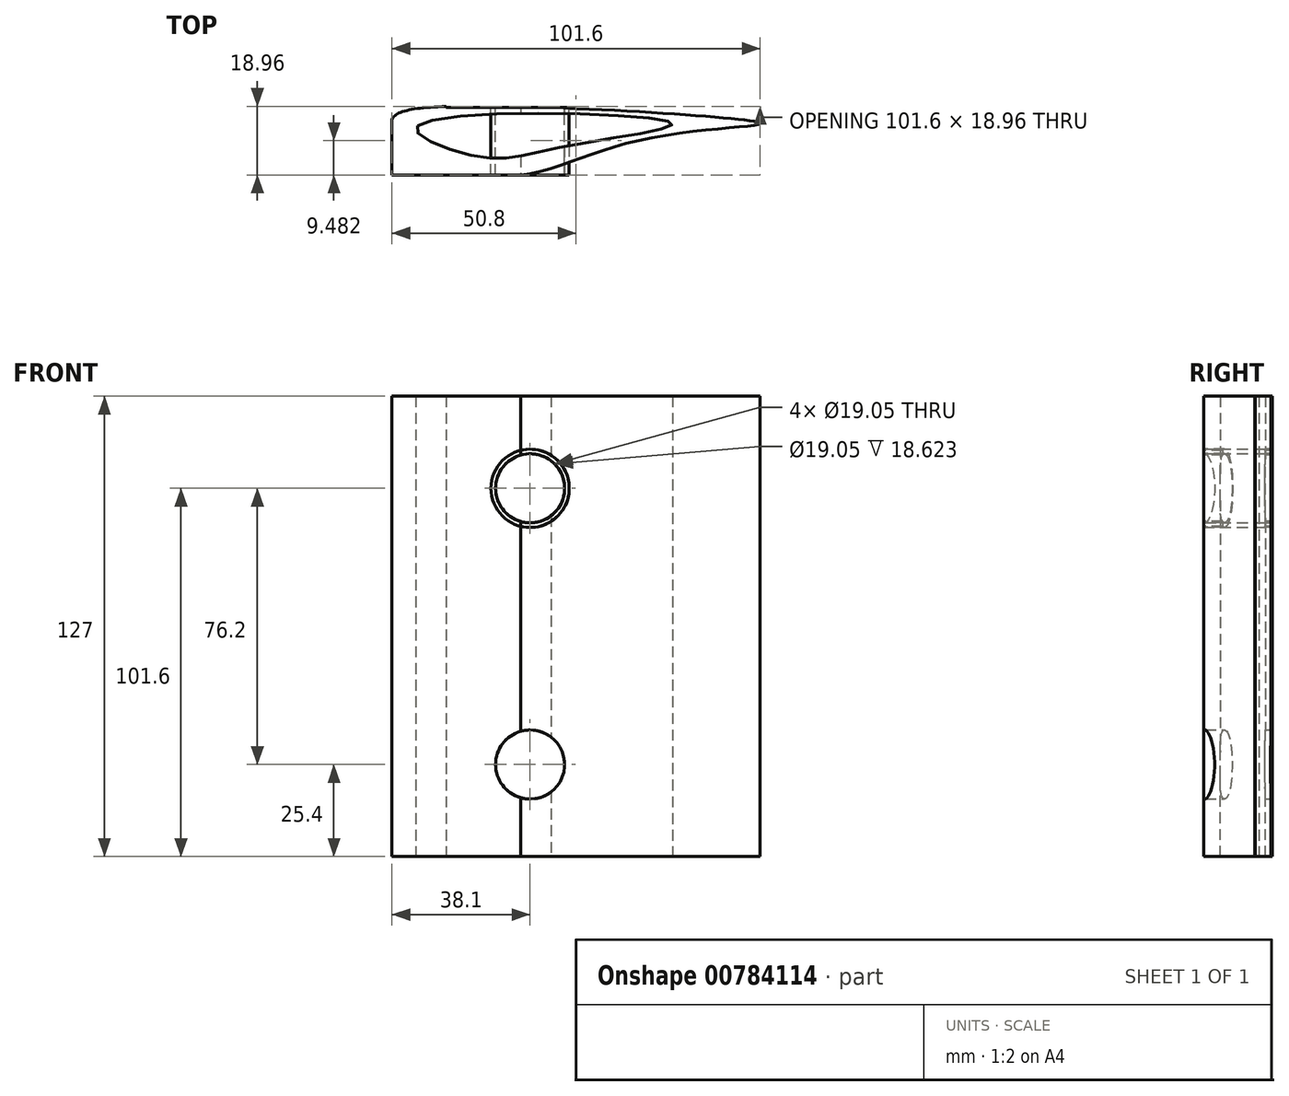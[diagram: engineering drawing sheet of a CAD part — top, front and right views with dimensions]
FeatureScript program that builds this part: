
annotation { "Feature Type Name" : "Feature", "Feature Type Description" : "" }
export const myFeature = defineFeature(function(context is Context, id is Id, definition is map)
    precondition{}
    {
        {
            var Q0;
            Q0=qCreatedBy(makeId("Front.planeOp"),FACE);
            var sketch = newSketch(context, id + "F0", { "sketchPlane" : qUnion([Q0])});
            skLineSegment(sketch, "E0.bottom", {"start": v(0, 0) * mm, "end": v(101.6, 0) * mm});
            skLineSegment(sketch, "E0.top", {"start": v(0, -127) * mm, "end": v(101.6, -127) * mm});
            skLineSegment(sketch, "E0.left", {"start": v(0, 0) * mm, "end": v(0, -127) * mm});
            skLineSegment(sketch, "E0.right", {"start": v(101.6, 0) * mm, "end": v(101.6, -127) * mm});
            skLineSegment(sketch, "E1", {"start": v(0, -127) * mm, "end": v(38.1, -127) * mm});
            skLineSegment(sketch, "E2", {"start": v(38.1, -127) * mm, "end": v(38.1, -101.6) * mm});
            skLineSegment(sketch, "E3", {"start": v(38.1, 0) * mm, "end": v(38.1, -25.4) * mm});
            skCircle(sketch, "E4", {"center": v(38.1, -25.4) * mm, "radius": 9.53 * mm});
            skCircle(sketch, "E5", {"center": v(38.1, -101.6) * mm, "radius": 9.53 * mm});
            skCircle(sketch, "E6", {"center": v(38.1, -25.4) * mm, "radius": 10.8 * mm});
            skCircle(sketch, "E7", {"center": v(38.1, -101.6) * mm, "radius": 10.8 * mm});
            skSolve(sketch);
        }
        {
            var Q0;
            Q0 = qSketchRegion(id + "F0", true);
            var Q1;
            Q1=makeQuery(id+"F0.imprint","IMPRINT",FACE,{"disambiguationData":[TD([[makeQuery(id+"F0.imprint","IMPRINT",EDGE,{"derivedFrom":sQuery(id+"F0.wireOp",EDGE,"E5")}),-1.0]])]});
            var Q2;
            Q2=makeQuery(id+"F0.imprint","IMPRINT",FACE,{"disambiguationData":[TD([[makeQuery(id+"F0.imprint","IMPRINT",EDGE,{"derivedFrom":sQuery(id+"F0.wireOp",EDGE,"E4")}),-1.0]])]});
            extrude(context, id + "F1", {"entities" : qUnion([Q0, Q1, Q2]), "depth" : 19.05 * mm, "offsetDistance" : 25.4 * mm});
        }
        {
            var Q0;
            Q0=makeQuery(id+"F0.imprint","IMPRINT",FACE,{"disambiguationData":[TD([[makeQuery(id+"F0.imprint","IMPRINT",EDGE,{"derivedFrom":sQuery(id+"F0.wireOp",EDGE,"E4")}),-1.0]])]});
            var Q1;
            Q1=makeQuery(id+"F0.imprint","IMPRINT",FACE,{"disambiguationData":[TD([[makeQuery(id+"F0.imprint","IMPRINT",EDGE,{"derivedFrom":sQuery(id+"F0.wireOp",EDGE,"E5")}),-1.0]])]});
            extrude(context, id + "F2", {"entities" : qUnion([Q0, Q1]), "operationType" : NewBodyOperationType.ADD, "oppositeDirection" : true, "depth" : 12.7 * mm, "offsetDistance" : 25.4 * mm, "hasSecondDirection" : true, "secondDirectionOppositeDirection" : false, "secondDirectionDepth" : 31.75 * mm});
        }
        {
            var Q0;
            Q0=makeQuery(id+"F1.opExtrude","SWEPT_FACE",FACE,{"disambiguationData":[OSD([sQuery(id+"F0.wireOp",EDGE,"E0.top"),sQuery(id+"F0.wireOp",EDGE,"E1")])]});
            var sketch = newSketch(context, id + "F3", { "sketchPlane" : qUnion([Q0])});
            skLineSegment(sketch, "E8", {"start": v(0, 9.53) * mm, "end": v(0, 0) * mm});
            skLineSegment(sketch, "E9", {"start": v(0, 0) * mm, "end": v(0, 4.76) * mm});
            skLineSegment(sketch, "E10", {"start": v(0, 4.76) * mm, "end": v(101.6, 4.76) * mm});
            skFitSpline(sketch, "E11", {"points": [v(0, 4.76) * mm, v(27, 19.05) * mm, v(67.8, 9.53) * mm, v(101.6, 4.76) * mm, v(26.4, 0) * mm, v(0, 4.76) * mm]});
            skSolve(sketch);
        }
        {
            var Q0;
            {var subQ0=sQuery(id+"F3.wireOp",EDGE,"E8");Q0=makeQuery(id+"F3.imprint","IMPRINT",FACE,{"disambiguationData":[TD([[makeQuery(id+"F3.imprint","IMPRINT",EDGE,{"derivedFrom":subQ0}),1.0]])]});}
            var Q1;
            {var subQ0=sQuery(id+"F3.wireOp",EDGE,"E9");var subQ3=sQuery(id+"F3.wireOp",EDGE,"E11");var subQ4=makeQuery(id+"F3.imprint","INTERSECT",VERTEX,{"derivedFrom":[subQ0,subQ3]});Q1=makeQuery(id+"F3.imprint","IMPRINT",FACE,{"disambiguationData":[TD([[makeQuery(id+"F3.imprint","IMPRINT",EDGE,{"disambiguationData":[TD([[subQ4,-1.0]])],"derivedFrom":subQ0}),1.0]])]});}
            var Q2;
            {var subQ0=sQuery(id+"F3.wireOp",EDGE,"E11");var subQ1=sQuery(id+"F0.wireOp",EDGE,"E0.top");var subQ2=makeQuery(id+"F1.opExtrude","CAP_EDGE",EDGE,{"disambiguationData":[OSD([subQ1,sQuery(id+"F0.wireOp",EDGE,"E1")])],"isStart":false});var subQ3=makeQuery(id+"F3.imprint","INTERSECT",VERTEX,{"disambiguationData":[OD(1.0)],"derivedFrom":[subQ2,subQ0]});Q2=makeQuery(id+"F3.imprint","IMPRINT",FACE,{"disambiguationData":[TD([[makeQuery(id+"F3.imprint","IMPRINT",EDGE,{"disambiguationData":[TD([[subQ3,-1.0]])],"derivedFrom":subQ0}),1.0]])]});}
            var Q3;
            {var subQ0=sQuery(id+"F3.wireOp",EDGE,"E11");var subQ1=sQuery(id+"F0.wireOp",EDGE,"E0.top");var subQ4=makeQuery(id+"F1.opExtrude","CAP_EDGE",EDGE,{"disambiguationData":[OSD([subQ1,sQuery(id+"F0.wireOp",EDGE,"E1")])],"isStart":true});var subQ5=makeQuery(id+"F3.imprint","INTERSECT",VERTEX,{"disambiguationData":[OD(0.0)],"derivedFrom":[subQ4,subQ0]});Q3=makeQuery(id+"F3.imprint","IMPRINT",FACE,{"disambiguationData":[TD([[makeQuery(id+"F3.imprint","IMPRINT",EDGE,{"disambiguationData":[TD([[subQ5,1.0]])],"derivedFrom":subQ0}),1.0]])]});}
            extrude(context, id + "F4", {"entities" : qUnion([Q0, Q1, Q2, Q3]), "operationType" : NewBodyOperationType.REMOVE, "endBound" : BoundingType.THROUGH_ALL, "oppositeDirection" : true, "depth" : 25.4 * mm, "offsetDistance" : 25.4 * mm});
        }
        {
            var Q0;
            {var subQ0=sQuery(id+"F0.wireOp",EDGE,"E5");var subQ1=sQuery(id+"F0.wireOp",EDGE,"E1");var subQ3=sQuery(id+"F0.wireOp",EDGE,"E0.top");var subQ4=sQuery(id+"F3.wireOp",EDGE,"E11");var subQ5=makeQuery(id+"F1.opExtrude","CAP_EDGE",EDGE,{"disambiguationData":[OSD([subQ3,subQ1])],"isStart":false});var subQ6=makeQuery(id+"F3.imprint","INTERSECT",VERTEX,{"disambiguationData":[OD(1.0)],"derivedFrom":[subQ5,subQ4]});Q0=makeQuery(id+"F4.boolean.opBoolean","COPY",FACE,{"disambiguationData":[TD([makeQuery(id+"F1.opExtrude","SWEPT_FACE",FACE,{"disambiguationData":[OSD([subQ0])]})])],"derivedFrom":makeQuery(id+"F4.opExtrude","SWEPT_FACE",FACE,{"disambiguationData":[OSD([subQ3,subQ1]),TDD([makeQuery(id+"F3.imprint","IMPRINT",EDGE,{"disambiguationData":[TD([[subQ6,-1.0]])],"derivedFrom":subQ5})])]})});}
            var sketch = newSketch(context, id + "F5", { "sketchPlane" : qUnion([Q0])});
            skSolve(sketch);
        }
        {
            var Q0;
            {var subQ1=sQuery(id+"F0.wireOp",EDGE,"E1");var subQ2=sQuery(id+"F0.wireOp",EDGE,"E0.top");var subQ3=makeQuery(id+"F1.opExtrude","CAP_EDGE",EDGE,{"disambiguationData":[OSD([subQ2,subQ1])],"isStart":false});var subQ6=sQuery(id+"F3.wireOp",EDGE,"E11");var subQ7=makeQuery(id+"F3.imprint","INTERSECT",VERTEX,{"disambiguationData":[OD(1.0)],"derivedFrom":[subQ3,subQ6]});var subQ8=makeQuery(id+"F4.opExtrude","SWEPT_FACE",FACE,{"disambiguationData":[OSD([subQ2,subQ1]),TDD([makeQuery(id+"F3.imprint","IMPRINT",EDGE,{"disambiguationData":[TD([[subQ7,-1.0]])],"derivedFrom":subQ3})])]});var subQ9=sQuery(id+"F0.wireOp",EDGE,"E5");var subQ11=makeQuery(id+"F2.opExtrude","SWEPT_FACE",FACE,{"disambiguationData":[OSD([subQ9])]});var subQ12=makeQuery(id+"F1.opExtrude","SWEPT_FACE",FACE,{"disambiguationData":[OSD([subQ9])]});Q0=makeQuery(id+"F5.imprint","IMPRINT",FACE,{"disambiguationData":[TD([[makeQuery(id+"F5.imprint","IMPRINT",EDGE,{"derivedFrom":makeQuery(id+"F4.boolean.opBoolean","INTERSECT",EDGE,{"derivedFrom":[makeQuery(id+"F2.boolean.opBoolean","MERGE",FACE,{"derivedFrom":[subQ12,subQ11]}),subQ8]})}),-1.0]])]});}
            var Q1;
            {var subQ0=sQuery(id+"F0.wireOp",EDGE,"E4");var subQ1=sQuery(id+"F0.wireOp",EDGE,"E1");var subQ3=sQuery(id+"F0.wireOp",EDGE,"E0.top");var subQ4=sQuery(id+"F3.wireOp",EDGE,"E11");var subQ5=makeQuery(id+"F1.opExtrude","CAP_EDGE",EDGE,{"disambiguationData":[OSD([subQ3,subQ1])],"isStart":false});var subQ6=makeQuery(id+"F3.imprint","INTERSECT",VERTEX,{"disambiguationData":[OD(1.0)],"derivedFrom":[subQ5,subQ4]});Q1=makeQuery(id+"F4.boolean.opBoolean","COPY",FACE,{"disambiguationData":[TD([makeQuery(id+"F1.opExtrude","SWEPT_FACE",FACE,{"disambiguationData":[OSD([subQ0])]})])],"derivedFrom":makeQuery(id+"F4.opExtrude","SWEPT_FACE",FACE,{"disambiguationData":[OSD([subQ3,subQ1]),TDD([makeQuery(id+"F3.imprint","IMPRINT",EDGE,{"disambiguationData":[TD([[subQ6,-1.0]])],"derivedFrom":subQ5})])]})});}
            extrude(context, id + "F6", {"entities" : qUnion([Q0, Q1]), "depth" : 25.4 * mm, "offsetDistance" : 25.4 * mm});
        }
        {
            var Q0;
            Q0=makeQuery(id+"F1.opExtrude","SWEPT_FACE",FACE,{"disambiguationData":[OSD([sQuery(id+"F0.wireOp",EDGE,"E0.top"),sQuery(id+"F0.wireOp",EDGE,"E1")])]});
            var sketch = newSketch(context, id + "F7", { "sketchPlane" : qUnion([Q0])});
            skFitSpline(sketch, "E12", {"points": [v(7.03, 5.45) * mm, v(23.26, 13.9) * mm, v(47.26, 11.22) * mm, v(77.04, 4.56) * mm, v(7.03, 5.45) * mm]});
            skSolve(sketch);
        }
        {
            var Q0;
            Q0 = qSketchRegion(id + "F7", true);
            extrude(context, id + "F8", {"entities" : qUnion([Q0]), "operationType" : NewBodyOperationType.REMOVE, "endBound" : BoundingType.THROUGH_ALL, "oppositeDirection" : true, "depth" : 25.4 * mm, "offsetDistance" : 25.4 * mm});
        }
        {
            var Q0;
            Q0=makeQuery(id+"F2.opExtrude","CAP_FACE",FACE,{"disambiguationData":[OSD([sQuery(id+"F0.wireOp",EDGE,"E5"),sQuery(id+"F0.wireOp",EDGE,"E7")])],"isStart":false});
            var sketch = newSketch(context, id + "F9", { "sketchPlane" : qUnion([Q0])});
            skSolve(sketch);
        }
        {
            var Q0;
            Q0=makeQuery(id+"F2.opExtrude","CAP_FACE",FACE,{"disambiguationData":[OSD([sQuery(id+"F0.wireOp",EDGE,"E4"),sQuery(id+"F0.wireOp",EDGE,"E6")])],"isStart":false});
            var Q1;
            Q1=makeQuery(id+"F9.imprint","IMPRINT",FACE,{"disambiguationData":[TD([[makeQuery(id+"F9.imprint","IMPRINT",EDGE,{"derivedFrom":makeQuery(id+"F2.opExtrude","CAP_EDGE",EDGE,{"disambiguationData":[OSD([sQuery(id+"F0.wireOp",EDGE,"E5")])],"isStart":false})}),1.0]])]});
            extrude(context, id + "F10", {"entities" : qUnion([Q0, Q1]), "oppositeDirection" : true, "depth" : 44.45 * mm, "offsetDistance" : 25.4 * mm});
        }
        {
            var Q0;
            Q0=makeQuery(id+"F1.opExtrude","SWEPT_FACE",FACE,{"disambiguationData":[OSD([sQuery(id+"F0.wireOp",EDGE,"E0.bottom")])]});
            var sketch = newSketch(context, id + "F11", { "sketchPlane" : qUnion([Q0])});
            skLineSegment(sketch, "E13.bottom", {"start": v(35.45, -19.05) * mm, "end": v(49.46, -19.05) * mm});
            skLineSegment(sketch, "E13.top", {"start": v(35.45, -32.26) * mm, "end": v(49.46, -32.26) * mm});
            skLineSegment(sketch, "E13.left", {"start": v(35.45, -19.05) * mm, "end": v(35.45, -32.26) * mm});
            skLineSegment(sketch, "E13.right", {"start": v(49.46, -19.05) * mm, "end": v(49.46, -32.26) * mm});
            skLineSegment(sketch, "E14.bottom", {"start": v(35.45, -19.05) * mm, "end": v(17.66, -19.05) * mm});
            skLineSegment(sketch, "E14.top", {"start": v(35.45, -34.67) * mm, "end": v(17.66, -34.67) * mm});
            skLineSegment(sketch, "E14.left", {"start": v(35.45, -19.05) * mm, "end": v(35.45, -34.67) * mm});
            skLineSegment(sketch, "E14.right", {"start": v(17.66, -19.05) * mm, "end": v(17.66, -34.67) * mm});
            skLineSegment(sketch, "E15.bottom", {"start": v(43.88, -0.43) * mm, "end": v(51.36, -0.43) * mm});
            skLineSegment(sketch, "E15.top", {"start": v(43.88, 15.43) * mm, "end": v(51.36, 15.43) * mm});
            skLineSegment(sketch, "E15.left", {"start": v(43.88, -0.43) * mm, "end": v(43.88, 15.43) * mm});
            skLineSegment(sketch, "E15.right", {"start": v(51.36, -0.43) * mm, "end": v(51.36, 15.43) * mm});
            skLineSegment(sketch, "E16.bottom", {"start": v(43.88, -0.43) * mm, "end": v(14.92, -0.43) * mm});
            skLineSegment(sketch, "E16.top", {"start": v(43.88, 24.97) * mm, "end": v(14.92, 24.97) * mm});
            skLineSegment(sketch, "E16.left", {"start": v(43.88, -0.43) * mm, "end": v(43.88, 24.97) * mm});
            skLineSegment(sketch, "E16.right", {"start": v(14.92, -0.43) * mm, "end": v(14.92, 24.97) * mm});
            skSolve(sketch);
        }
        {
            var Q0;
            Q0 = qSketchRegion(id + "F11", true);
            extrude(context, id + "F12", {"entities" : qUnion([Q0]), "operationType" : NewBodyOperationType.REMOVE, "endBound" : BoundingType.THROUGH_ALL, "oppositeDirection" : true, "depth" : 25.4 * mm, "offsetDistance" : 25.4 * mm});
        }
    });
